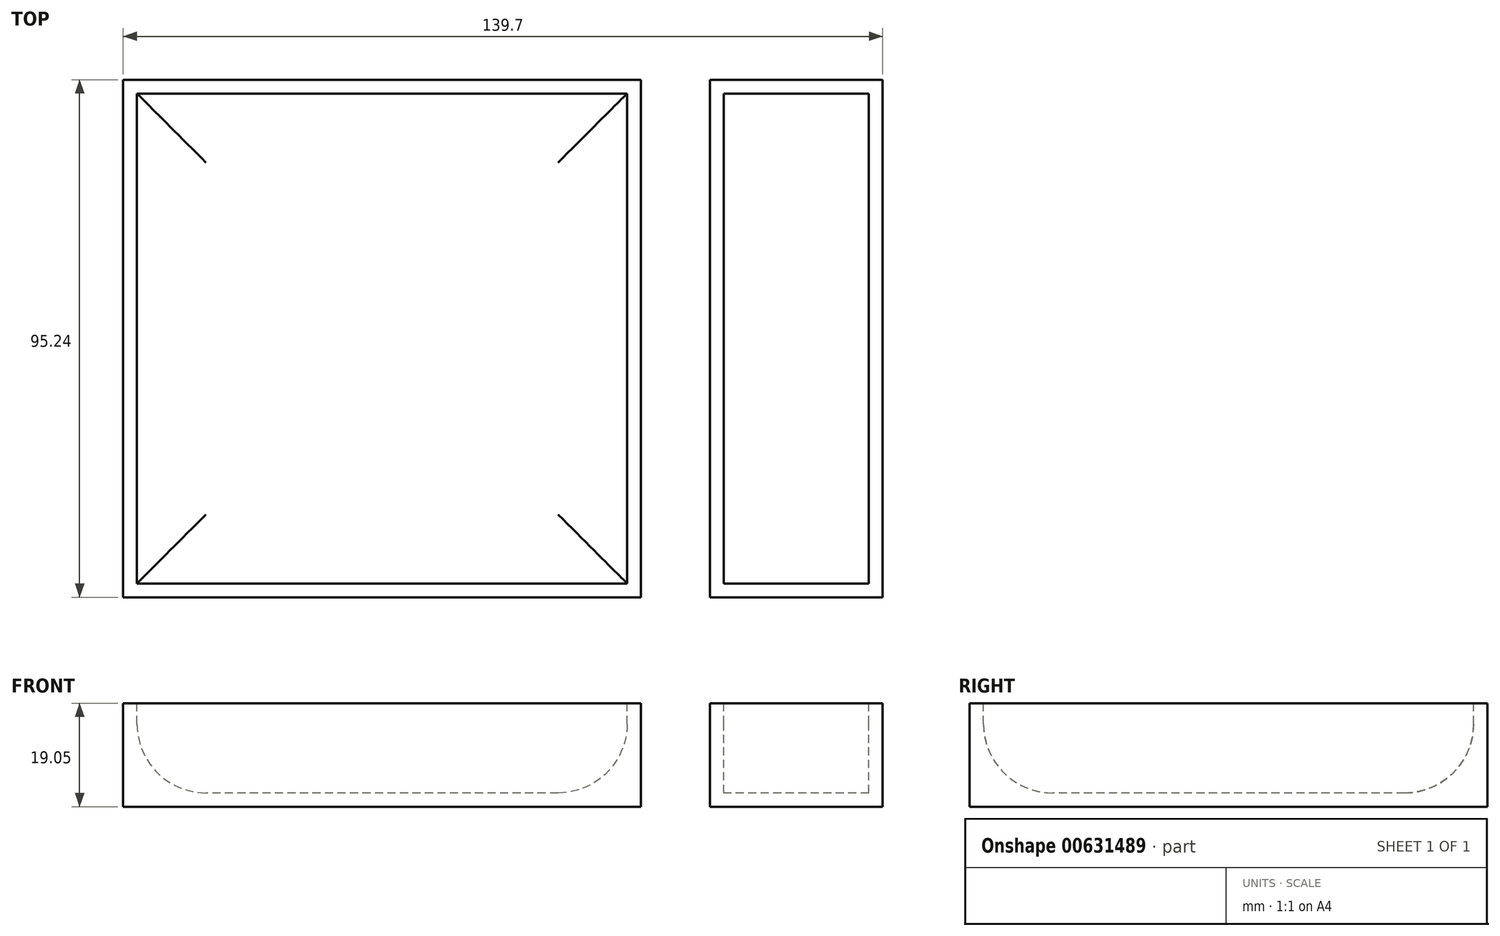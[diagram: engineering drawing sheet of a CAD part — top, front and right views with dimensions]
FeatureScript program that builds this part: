
annotation { "Feature Type Name" : "Feature", "Feature Type Description" : "" }
export const myFeature = defineFeature(function(context is Context, id is Id, definition is map)
    precondition{}
    {
        {
            var Q0;
            Q0=qCreatedBy(makeId("Top.planeOp"),FACE);
            var sketch = newSketch(context, id + "F0", { "sketchPlane" : qUnion([Q0])});
            skLineSegment(sketch, "E0.bottom", {"start": v(47.63, 47.63) * mm, "end": v(-47.63, 47.63) * mm});
            skLineSegment(sketch, "E0.top", {"start": v(47.63, -47.63) * mm, "end": v(-47.63, -47.63) * mm});
            skLineSegment(sketch, "E0.left", {"start": v(47.63, 47.63) * mm, "end": v(47.63, -47.63) * mm});
            skLineSegment(sketch, "E0.right", {"start": v(-47.63, 47.63) * mm, "end": v(-47.63, -47.62) * mm});
            skPoint(sketch, "E0.middle", {"position": v(0, 0) * mm});
            skLineSegment(sketch, "E1.bottom", {"start": v(92.08, 47.63) * mm, "end": v(60.33, 47.63) * mm});
            skLineSegment(sketch, "E1.top", {"start": v(92.08, -47.62) * mm, "end": v(60.33, -47.62) * mm});
            skLineSegment(sketch, "E1.left", {"start": v(92.08, 47.63) * mm, "end": v(92.08, -47.63) * mm});
            skLineSegment(sketch, "E1.right", {"start": v(60.33, 47.63) * mm, "end": v(60.33, -47.63) * mm});
            skPoint(sketch, "E1.middle", {"position": v(76.2, 0) * mm});
            skSolve(sketch);
        }
        {
            var Q0;
            Q0=makeQuery(id+"F0.imprint","IMPRINT",FACE,{"disambiguationData":[TD([[makeQuery(id+"F0.imprint","IMPRINT",EDGE,{"derivedFrom":sQuery(id+"F0.wireOp",EDGE,"E0.bottom")}),1.0]])]});
            var Q1;
            Q1=makeQuery(id+"F0.imprint","IMPRINT",FACE,{"disambiguationData":[TD([[makeQuery(id+"F0.imprint","IMPRINT",EDGE,{"derivedFrom":sQuery(id+"F0.wireOp",EDGE,"E1.bottom")}),1.0]])]});
            extrude(context, id + "F1", {"entities" : qUnion([Q0, Q1]), "depth" : 19.05 * mm, "offsetDistance" : 25.4 * mm});
        }
        {
            var Q0;
            Q0=makeQuery(id+"F1.opExtrude","CAP_FACE",FACE,{"disambiguationData":[OSD([sQuery(id+"F0.wireOp",EDGE,"E0.bottom"),sQuery(id+"F0.wireOp",EDGE,"E0.top"),sQuery(id+"F0.wireOp",EDGE,"E0.left"),sQuery(id+"F0.wireOp",EDGE,"E0.right")])],"isStart":false});
            var sketch = newSketch(context, id + "F2", { "sketchPlane" : qUnion([Q0])});
            skLineSegment(sketch, "E2.bottom", {"start": v(45.08, 45.08) * mm, "end": v(-45.09, 45.08) * mm});
            skLineSegment(sketch, "E2.top", {"start": v(45.09, -45.09) * mm, "end": v(-45.08, -45.09) * mm});
            skLineSegment(sketch, "E2.left", {"start": v(45.08, 45.08) * mm, "end": v(45.09, -45.09) * mm});
            skLineSegment(sketch, "E2.right", {"start": v(-45.09, 45.08) * mm, "end": v(-45.08, -45.09) * mm});
            skPoint(sketch, "E2.middle", {"position": v(0, 0) * mm});
            skLineSegment(sketch, "E3.bottom", {"start": v(89.53, 45.08) * mm, "end": v(62.86, 45.08) * mm});
            skLineSegment(sketch, "E3.top", {"start": v(89.53, -45.09) * mm, "end": v(62.86, -45.09) * mm});
            skLineSegment(sketch, "E3.left", {"start": v(89.53, 45.08) * mm, "end": v(89.53, -45.09) * mm});
            skLineSegment(sketch, "E3.right", {"start": v(62.86, 45.08) * mm, "end": v(62.86, -45.09) * mm});
            skPoint(sketch, "E3.middle", {"position": v(76.2, 0) * mm});
            skSolve(sketch);
        }
        {
            var Q0;
            Q0 = qSketchRegion(id + "F2", true);
            extrude(context, id + "F3", {"entities" : qUnion([Q0]), "operationType" : NewBodyOperationType.REMOVE, "oppositeDirection" : true, "depth" : 16.5 * mm, "offsetDistance" : 25.4 * mm});
        }
        {
            var Q0;
            Q0=makeQuery(id+"F3.boolean.opBoolean","COPY",FACE,{"derivedFrom":makeQuery(id+"F3.opExtrude","CAP_FACE",FACE,{"disambiguationData":[OSD([sQuery(id+"F2.wireOp",EDGE,"E2.bottom"),sQuery(id+"F2.wireOp",EDGE,"E2.top"),sQuery(id+"F2.wireOp",EDGE,"E2.left"),sQuery(id+"F2.wireOp",EDGE,"E2.right")])],"isStart":false})});
            var Q1;
            Q1=makeQuery(id+"F3.boolean.opBoolean","COPY",EDGE,{"derivedFrom":makeQuery(id+"F3.opExtrude","CAP_EDGE",EDGE,{"disambiguationData":[OSD([sQuery(id+"F2.wireOp",EDGE,"E3.bottom")])],"isStart":false})});
            var Q2;
            Q2=makeQuery(id+"F3.boolean.opBoolean","COPY",EDGE,{"derivedFrom":makeQuery(id+"F3.opExtrude","CAP_EDGE",EDGE,{"disambiguationData":[OSD([sQuery(id+"F2.wireOp",EDGE,"E3.top")])],"isStart":false})});
            fillet(context, id + "F4", {"entities" : qUnion([Q0, Q1, Q2]), "radius" : 12.7 * mm, "tangentPropagation" : true, "allowEdgeOverflow" : false});
        }
    });
